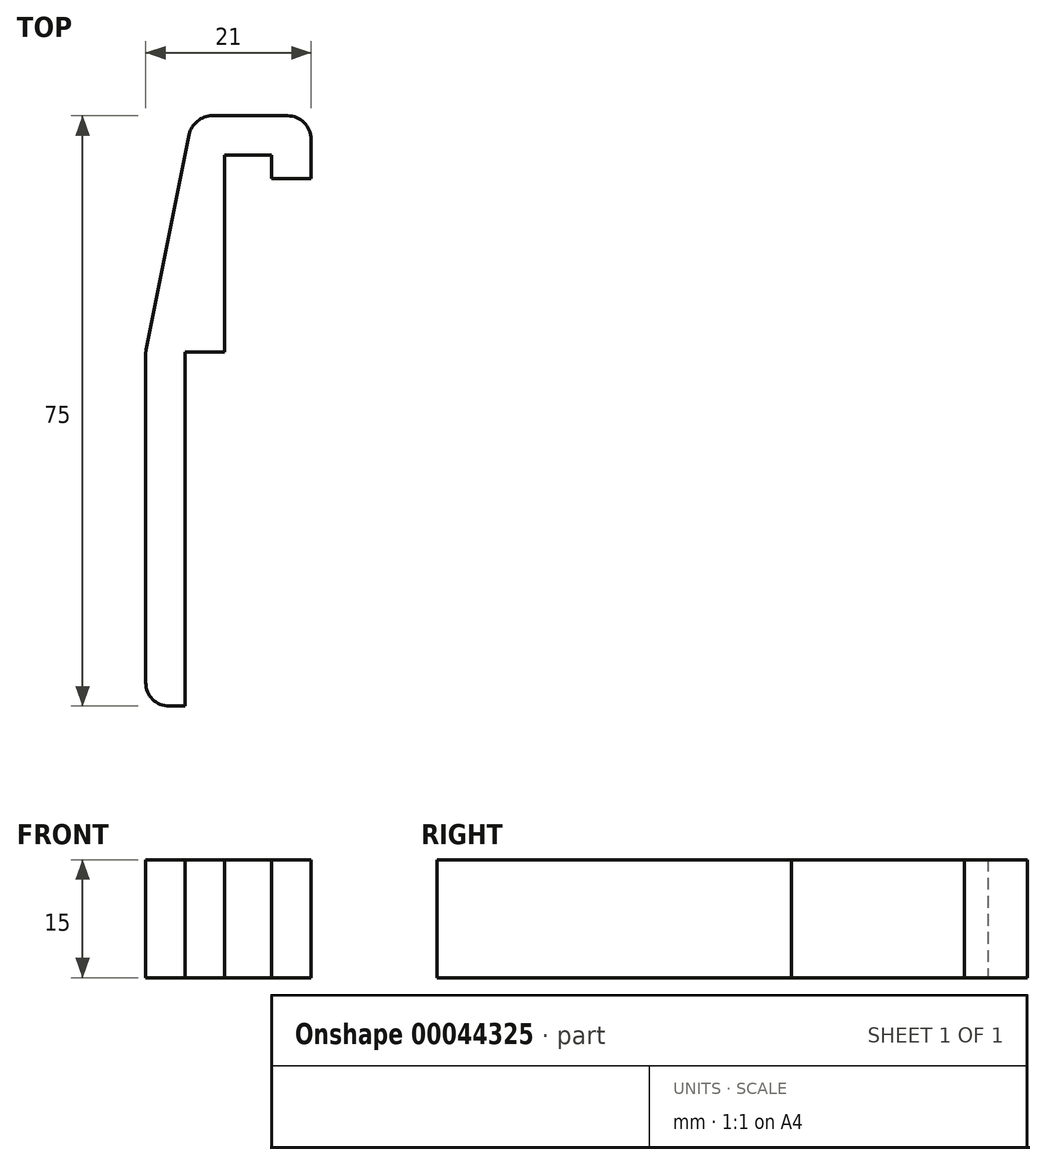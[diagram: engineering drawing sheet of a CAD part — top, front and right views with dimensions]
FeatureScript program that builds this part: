
annotation { "Feature Type Name" : "Feature", "Feature Type Description" : "" }
export const myFeature = defineFeature(function(context is Context, id is Id, definition is map)
    precondition{}
    {
        {
            var Q0;
            Q0=qCreatedBy(makeId("Top.planeOp"),FACE);
            var sketch = newSketch(context, id + "F0", { "sketchPlane" : qUnion([Q0])});
            skLineSegment(sketch, "E0", {"start": v(-2, -45) * mm, "end": v(0, -45) * mm});
            skLineSegment(sketch, "E1", {"start": v(0, -45) * mm, "end": v(0, 0) * mm});
            skLineSegment(sketch, "E2", {"start": v(0, 0) * mm, "end": v(5, 0) * mm});
            skLineSegment(sketch, "E3", {"start": v(5, 0) * mm, "end": v(5, 25) * mm});
            skLineSegment(sketch, "E4", {"start": v(5, 25) * mm, "end": v(11, 25) * mm});
            skLineSegment(sketch, "E5", {"start": v(11, 25) * mm, "end": v(11, 22) * mm});
            skLineSegment(sketch, "E6", {"start": v(11, 22) * mm, "end": v(16, 22) * mm});
            skLineSegment(sketch, "E7", {"start": v(16, 22) * mm, "end": v(16, 27) * mm});
            skLineSegment(sketch, "E8", {"start": v(16, 30) * mm, "end": v(1, 30) * mm});
            skLineSegment(sketch, "E9", {"start": v(-5, -0.3) * mm, "end": v(-5, -42) * mm});
            skLineSegment(sketch, "E10", {"start": v(13, 30) * mm, "end": v(3.46, 30) * mm});
            skLineSegment(sketch, "E11", {"start": v(0.52, 27.59) * mm, "end": v(-4.94, 0.3) * mm});
            skPoint(sketch, "E12.visualSharp", {"position": v(1, 30) * mm});
            skArc(sketch, "E12.filletArc", {"start": v(3.46, 30) * mm, "mid": v(1.56, 29.32) * mm, "end": v(0.52, 27.59) * mm});
            skPoint(sketch, "E13.visualSharp", {"position": v(-5, 0) * mm});
            skArc(sketch, "E13.filletArc", {"start": v(-4.94, 0.3) * mm, "mid": v(-4.99, 0) * mm, "end": v(-5, -0.3) * mm});
            skPoint(sketch, "E14.visualSharp", {"position": v(-5, -45) * mm});
            skArc(sketch, "E14.filletArc", {"start": v(-5, -42) * mm, "mid": v(-4.12, -44.12) * mm, "end": v(-2, -45) * mm});
            skPoint(sketch, "E15.visualSharp", {"position": v(16, 30) * mm});
            skArc(sketch, "E15.filletArc", {"start": v(16, 27) * mm, "mid": v(15.12, 29.12) * mm, "end": v(13, 30) * mm});
            skSolve(sketch);
        }
        {
            var Q0;
            Q0 = qSketchRegion(id + "F0", true);
            extrude(context, id + "F1", {"entities" : qUnion([Q0]), "depth" : 15 * mm});
        }
    });
